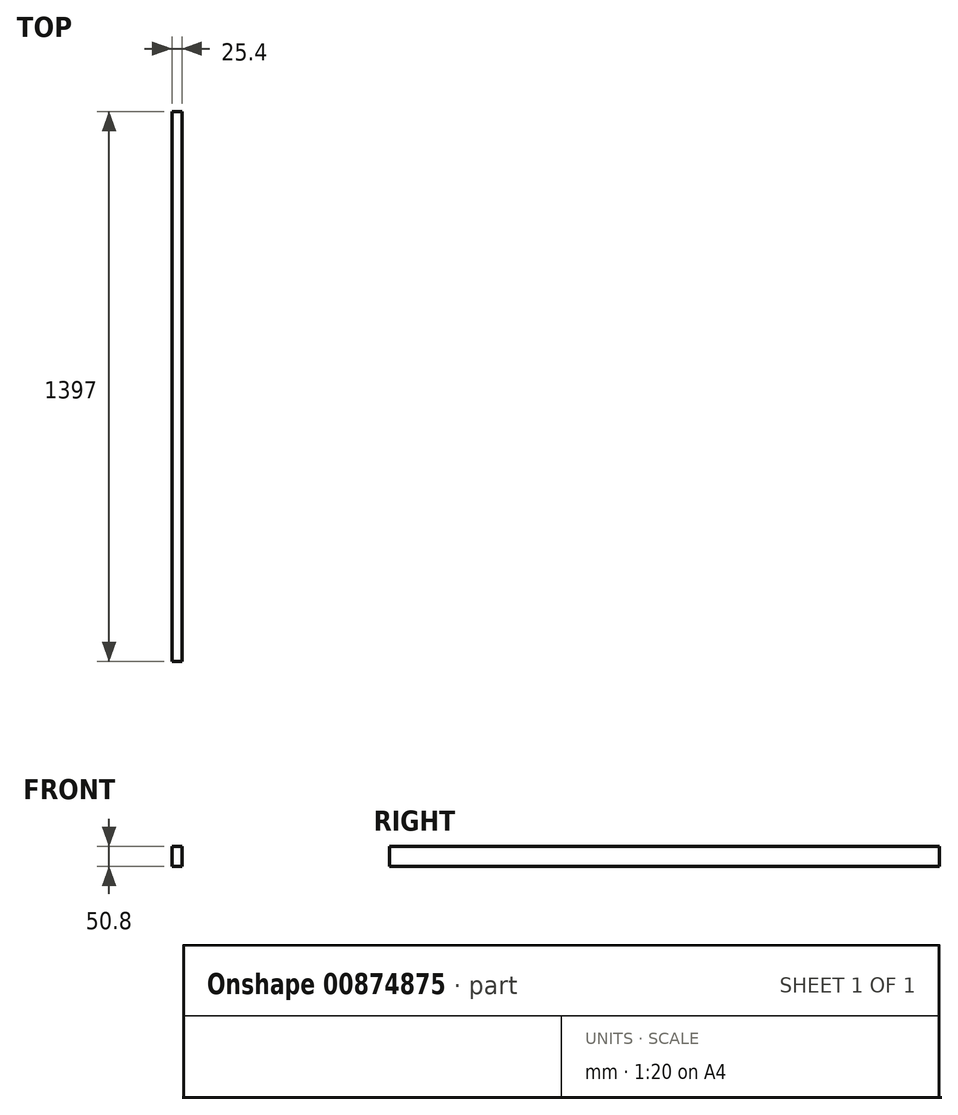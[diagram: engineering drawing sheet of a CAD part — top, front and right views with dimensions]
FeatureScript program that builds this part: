
annotation { "Feature Type Name" : "Feature", "Feature Type Description" : "" }
export const myFeature = defineFeature(function(context is Context, id is Id, definition is map)
    precondition{}
    {
        {
            var Q0;
            Q0=qCreatedBy(makeId("Front.planeOp"),FACE);
            var sketch = newSketch(context, id + "F0", { "sketchPlane" : qUnion([Q0])});
            skLineSegment(sketch, "E0.bottom", {"start": v(-52.15, 43.04) * mm, "end": v(-26.75, 43.04) * mm});
            skLineSegment(sketch, "E0.top", {"start": v(-52.15, -7.76) * mm, "end": v(-26.75, -7.76) * mm});
            skLineSegment(sketch, "E0.left", {"start": v(-52.15, 43.04) * mm, "end": v(-52.15, -7.76) * mm});
            skLineSegment(sketch, "E0.right", {"start": v(-26.75, 43.04) * mm, "end": v(-26.75, -7.76) * mm});
            skSolve(sketch);
        }
        {
            var Q0;
            Q0 = qSketchRegion(id + "F0", true);
            extrude(context, id + "F1", {"entities" : qUnion([Q0]), "depth" : 1397 * mm, "offsetDistance" : 25.4 * mm});
        }
    });
